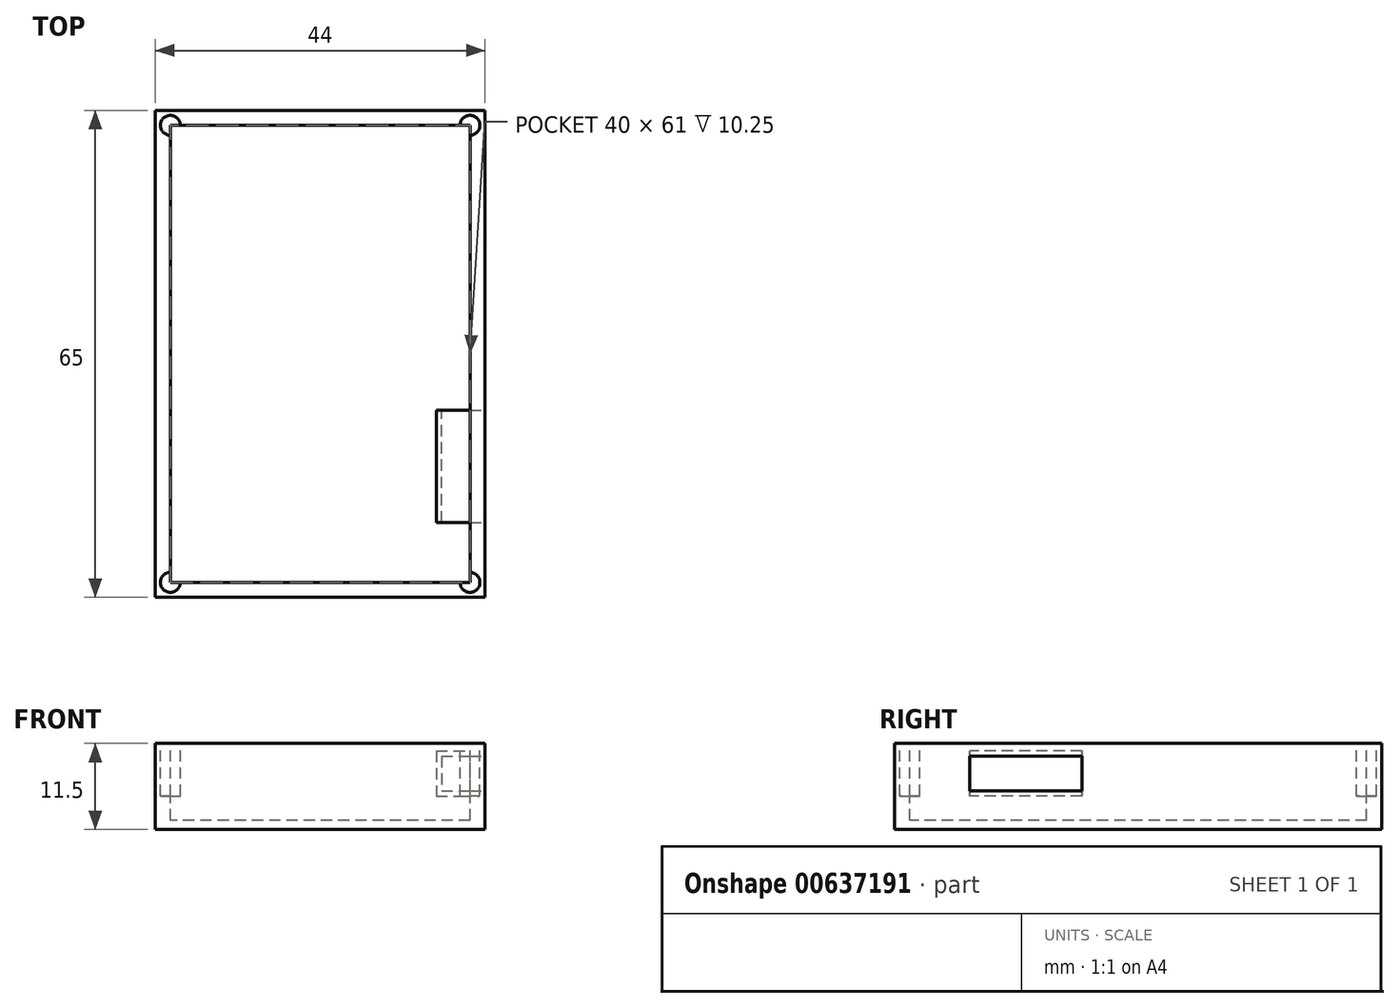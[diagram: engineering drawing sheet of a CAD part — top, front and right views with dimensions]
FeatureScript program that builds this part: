
annotation { "Feature Type Name" : "Feature", "Feature Type Description" : "" }
export const myFeature = defineFeature(function(context is Context, id is Id, definition is map)
    precondition{}
    {
        {
            var Q0;
            Q0=qCreatedBy(makeId("Top.planeOp"),FACE);
            var sketch = newSketch(context, id + "F0", { "sketchPlane" : qUnion([Q0])});
            skLineSegment(sketch, "E0.bottom", {"start": v(-22, 32.5) * mm, "end": v(22, 32.5) * mm});
            skLineSegment(sketch, "E0.top", {"start": v(-22, -32.5) * mm, "end": v(22, -32.5) * mm});
            skLineSegment(sketch, "E0.left", {"start": v(-22, 32.5) * mm, "end": v(-22, -32.5) * mm});
            skLineSegment(sketch, "E0.right", {"start": v(22, 32.5) * mm, "end": v(22, -32.5) * mm});
            skPoint(sketch, "E0.middle", {"position": v(0, 0) * mm});
            skSolve(sketch);
        }
        {
            var Q0;
            Q0 = qSketchRegion(id + "F0", true);
            extrude(context, id + "F1", {"entities" : qUnion([Q0]), "depth" : 11.5 * mm, "offsetDistance" : 25 * mm});
        }
        {
            var Q0;
            Q0=makeQuery(id+"F1.opExtrude","CAP_FACE",FACE,{"disambiguationData":[OSD([sQuery(id+"F0.wireOp",EDGE,"E0.bottom"),sQuery(id+"F0.wireOp",EDGE,"E0.top"),sQuery(id+"F0.wireOp",EDGE,"E0.left"),sQuery(id+"F0.wireOp",EDGE,"E0.right")])],"isStart":false});
            var sketch = newSketch(context, id + "F2", { "sketchPlane" : qUnion([Q0])});
            skLineSegment(sketch, "E1.bottom", {"start": v(20, 30.5) * mm, "end": v(-20, 30.5) * mm});
            skLineSegment(sketch, "E1.top", {"start": v(20, -30.5) * mm, "end": v(-20, -30.5) * mm});
            skLineSegment(sketch, "E1.left", {"start": v(20, 30.5) * mm, "end": v(20, -30.5) * mm});
            skLineSegment(sketch, "E1.right", {"start": v(-20, 30.5) * mm, "end": v(-20, -30.5) * mm});
            skPoint(sketch, "E1.middle", {"position": v(0, 0) * mm});
            skSolve(sketch);
        }
        {
            var Q0;
            Q0=makeQuery(id+"F2.imprint","IMPRINT",FACE,{"disambiguationData":[TD([[makeQuery(id+"F2.imprint","IMPRINT",EDGE,{"derivedFrom":sQuery(id+"F2.wireOp",EDGE,"E1.bottom")}),1.0]])]});
            extrude(context, id + "F3", {"entities" : qUnion([Q0]), "operationType" : NewBodyOperationType.REMOVE, "oppositeDirection" : true, "depth" : 10.25 * mm, "offsetDistance" : 25 * mm});
        }
        {
            var Q0;
            Q0=makeQuery(id+"F1.opExtrude","CAP_FACE",FACE,{"disambiguationData":[OSD([sQuery(id+"F0.wireOp",EDGE,"E0.bottom"),sQuery(id+"F0.wireOp",EDGE,"E0.top"),sQuery(id+"F0.wireOp",EDGE,"E0.left"),sQuery(id+"F0.wireOp",EDGE,"E0.right")])],"isStart":false});
            var sketch = newSketch(context, id + "F4", { "sketchPlane" : qUnion([Q0])});
            skCircle(sketch, "E2", {"center": v(-20, 30.5) * mm, "radius": 2 * mm});
            skCircle(sketch, "E3", {"center": v(-20, -30.5) * mm, "radius": 2 * mm});
            skCircle(sketch, "E4", {"center": v(20, -30.5) * mm, "radius": 2 * mm});
            skCircle(sketch, "E5", {"center": v(20, 30.5) * mm, "radius": 2 * mm});
            skSolve(sketch);
        }
        {
            var Q0;
            {var subQ0=sQuery(id+"F4.wireOp",EDGE,"E4");var subQ1=makeQuery(id+"F3.boolean.opBoolean","COPY",EDGE,{"derivedFrom":makeQuery(id+"F3.opExtrude","CAP_EDGE",EDGE,{"disambiguationData":[OSD([sQuery(id+"F2.wireOp",EDGE,"E1.left")])],"isStart":true})});var subQ2=makeQuery(id+"F4.imprint","INTERSECT",VERTEX,{"derivedFrom":[subQ1,subQ0]});Q0=makeQuery(id+"F4.imprint","IMPRINT",FACE,{"disambiguationData":[TD([[makeQuery(id+"F4.imprint","IMPRINT",EDGE,{"disambiguationData":[TD([[subQ2,-1.0]])],"derivedFrom":subQ0}),1.0]])]});}
            var Q1;
            {var subQ0=sQuery(id+"F4.wireOp",EDGE,"E3");var subQ1=makeQuery(id+"F3.boolean.opBoolean","COPY",EDGE,{"derivedFrom":makeQuery(id+"F3.opExtrude","CAP_EDGE",EDGE,{"disambiguationData":[OSD([sQuery(id+"F2.wireOp",EDGE,"E1.right")])],"isStart":true})});var subQ2=makeQuery(id+"F4.imprint","INTERSECT",VERTEX,{"derivedFrom":[subQ1,subQ0]});Q1=makeQuery(id+"F4.imprint","IMPRINT",FACE,{"disambiguationData":[TD([[makeQuery(id+"F4.imprint","IMPRINT",EDGE,{"disambiguationData":[TD([[subQ2,1.0]])],"derivedFrom":subQ0}),1.0]])]});}
            var Q2;
            {var subQ0=sQuery(id+"F4.wireOp",EDGE,"E5");var subQ1=makeQuery(id+"F3.boolean.opBoolean","COPY",EDGE,{"derivedFrom":makeQuery(id+"F3.opExtrude","CAP_EDGE",EDGE,{"disambiguationData":[OSD([sQuery(id+"F2.wireOp",EDGE,"E1.bottom")])],"isStart":true})});var subQ2=makeQuery(id+"F4.imprint","INTERSECT",VERTEX,{"derivedFrom":[subQ1,subQ0]});Q2=makeQuery(id+"F4.imprint","IMPRINT",FACE,{"disambiguationData":[TD([[makeQuery(id+"F4.imprint","IMPRINT",EDGE,{"disambiguationData":[TD([[subQ2,-1.0]])],"derivedFrom":subQ0}),1.0]])]});}
            var Q3;
            {var subQ0=sQuery(id+"F4.wireOp",EDGE,"E2");var subQ1=makeQuery(id+"F3.boolean.opBoolean","COPY",EDGE,{"derivedFrom":makeQuery(id+"F3.opExtrude","CAP_EDGE",EDGE,{"disambiguationData":[OSD([sQuery(id+"F2.wireOp",EDGE,"E1.bottom")])],"isStart":true})});var subQ2=makeQuery(id+"F4.imprint","INTERSECT",VERTEX,{"derivedFrom":[subQ1,subQ0]});Q3=makeQuery(id+"F4.imprint","IMPRINT",FACE,{"disambiguationData":[TD([[makeQuery(id+"F4.imprint","IMPRINT",EDGE,{"disambiguationData":[TD([[subQ2,1.0]])],"derivedFrom":subQ0}),1.0]])]});}
            extrude(context, id + "F5", {"entities" : qUnion([Q0, Q1, Q2, Q3]), "operationType" : NewBodyOperationType.ADD, "oppositeDirection" : true, "depth" : 11 * mm, "offsetDistance" : 25 * mm});
        }
        {
            var Q0;
            Q0=makeQuery(id+"F5.boolean.opBoolean","MERGE",FACE,{"derivedFrom":[makeQuery(id+"F1.opExtrude","CAP_FACE",FACE,{"disambiguationData":[OSD([sQuery(id+"F0.wireOp",EDGE,"E0.bottom"),sQuery(id+"F0.wireOp",EDGE,"E0.top"),sQuery(id+"F0.wireOp",EDGE,"E0.left"),sQuery(id+"F0.wireOp",EDGE,"E0.right")])],"isStart":false}),makeQuery(id+"F5.opExtrude","CAP_FACE",FACE,{"disambiguationData":[OSD([sQuery(id+"F4.wireOp",EDGE,"E2")])],"isStart":true}),makeQuery(id+"F5.opExtrude","CAP_FACE",FACE,{"disambiguationData":[OSD([sQuery(id+"F4.wireOp",EDGE,"E3")])],"isStart":true}),makeQuery(id+"F5.opExtrude","CAP_FACE",FACE,{"disambiguationData":[OSD([sQuery(id+"F4.wireOp",EDGE,"E4")])],"isStart":true}),makeQuery(id+"F5.opExtrude","CAP_FACE",FACE,{"disambiguationData":[OSD([sQuery(id+"F4.wireOp",EDGE,"E5")])],"isStart":true})]});
            var sketch = newSketch(context, id + "F6", { "sketchPlane" : qUnion([Q0])});
            skCircle(sketch, "E6", {"center": v(-20, 30.5) * mm, "radius": 1.32 * mm});
            skCircle(sketch, "E7", {"center": v(-20, -30.5) * mm, "radius": 1.32 * mm});
            skCircle(sketch, "E8", {"center": v(20, -30.5) * mm, "radius": 1.32 * mm});
            skCircle(sketch, "E9", {"center": v(20, 30.5) * mm, "radius": 1.32 * mm});
            skSolve(sketch);
        }
        {
            var Q0;
            Q0=makeQuery(id+"F6.imprint","IMPRINT",FACE,{"disambiguationData":[TD([[makeQuery(id+"F6.imprint","IMPRINT",EDGE,{"derivedFrom":sQuery(id+"F6.wireOp",EDGE,"E7")}),1.0]])]});
            var Q1;
            Q1=makeQuery(id+"F6.imprint","IMPRINT",FACE,{"disambiguationData":[TD([[makeQuery(id+"F6.imprint","IMPRINT",EDGE,{"derivedFrom":sQuery(id+"F6.wireOp",EDGE,"E6")}),1.0]])]});
            var Q2;
            Q2=makeQuery(id+"F6.imprint","IMPRINT",FACE,{"disambiguationData":[TD([[makeQuery(id+"F6.imprint","IMPRINT",EDGE,{"derivedFrom":sQuery(id+"F6.wireOp",EDGE,"E9")}),1.0]])]});
            var Q3;
            Q3=makeQuery(id+"F6.imprint","IMPRINT",FACE,{"disambiguationData":[TD([[makeQuery(id+"F6.imprint","IMPRINT",EDGE,{"derivedFrom":sQuery(id+"F6.wireOp",EDGE,"E8")}),1.0]])]});
            extrude(context, id + "F7", {"entities" : qUnion([Q0, Q1, Q2, Q3]), "operationType" : NewBodyOperationType.REMOVE, "oppositeDirection" : true, "depth" : 7 * mm, "offsetDistance" : 25 * mm});
        }
        {
            var Q0;
            Q0=makeQuery(id+"F1.opExtrude","SWEPT_FACE",FACE,{"disambiguationData":[OSD([sQuery(id+"F0.wireOp",EDGE,"E0.left")])]});
            var sketch = newSketch(context, id + "F9", { "sketchPlane" : qUnion([Q0])});
            skSolve(sketch);
        }
        {
            var Q0;
            Q0=makeQuery(id+"F1.opExtrude","SWEPT_FACE",FACE,{"disambiguationData":[OSD([sQuery(id+"F0.wireOp",EDGE,"E0.right")])]});
            var sketch = newSketch(context, id + "F10", { "sketchPlane" : qUnion([Q0])});
            skLineSegment(sketch, "E10.bottom", {"start": v(-22.5, 10.5) * mm, "end": v(-7.5, 10.5) * mm});
            skLineSegment(sketch, "E10.top", {"start": v(-22.5, 4.5) * mm, "end": v(-7.5, 4.5) * mm});
            skLineSegment(sketch, "E10.left", {"start": v(-22.5, 10.5) * mm, "end": v(-22.5, 4.5) * mm});
            skLineSegment(sketch, "E10.right", {"start": v(-7.5, 10.5) * mm, "end": v(-7.5, 4.5) * mm});
            skPoint(sketch, "E11.oppositeSnap0", {"position": v(-15, 10.5) * mm});
            skLineSegment(sketch, "E11.bottom", {"start": v(-15, 10.5) * mm, "end": v(-15, 10.5) * mm});
            skSolve(sketch);
        }
        {
            var Q0;
            Q0=makeQuery(id+"F10.imprint","IMPRINT",FACE,{"disambiguationData":[TD([[makeQuery(id+"F10.imprint","IMPRINT",EDGE,{"derivedFrom":sQuery(id+"F10.wireOp",EDGE,"E10.bottom")}),-1.0]])]});
            extrude(context, id + "F11", {"entities" : qUnion([Q0]), "operationType" : NewBodyOperationType.ADD, "oppositeDirection" : true, "depth" : 6.5 * mm, "offsetDistance" : 25 * mm});
        }
        {
            var Q0;
            Q0=makeQuery(id+"F11.opExtrude","SWEPT_FACE",FACE,{"disambiguationData":[OSD([sQuery(id+"F10.wireOp",EDGE,"E10.right")])]});
            var sketch = newSketch(context, id + "F12", { "sketchPlane" : qUnion([Q0])});
            skLineSegment(sketch, "E12.bottom", {"start": v(-16.2, 9.8) * mm, "end": v(-23.2, 9.8) * mm});
            skLineSegment(sketch, "E12.top", {"start": v(-16.2, 5.2) * mm, "end": v(-23.2, 5.2) * mm});
            skLineSegment(sketch, "E12.left", {"start": v(-16.2, 9.8) * mm, "end": v(-16.2, 5.2) * mm});
            skLineSegment(sketch, "E12.right", {"start": v(-23.2, 9.8) * mm, "end": v(-23.2, 5.2) * mm});
            skPoint(sketch, "E12.middle", {"position": v(-19.7, 7.5) * mm});
            skSolve(sketch);
        }
        {
            var Q0;
            Q0 = qSketchRegion(id + "F12", true);
            extrude(context, id + "F13", {"entities" : qUnion([Q0]), "operationType" : NewBodyOperationType.REMOVE, "oppositeDirection" : true, "depth" : 15 * mm, "offsetDistance" : 25 * mm});
        }
    });
